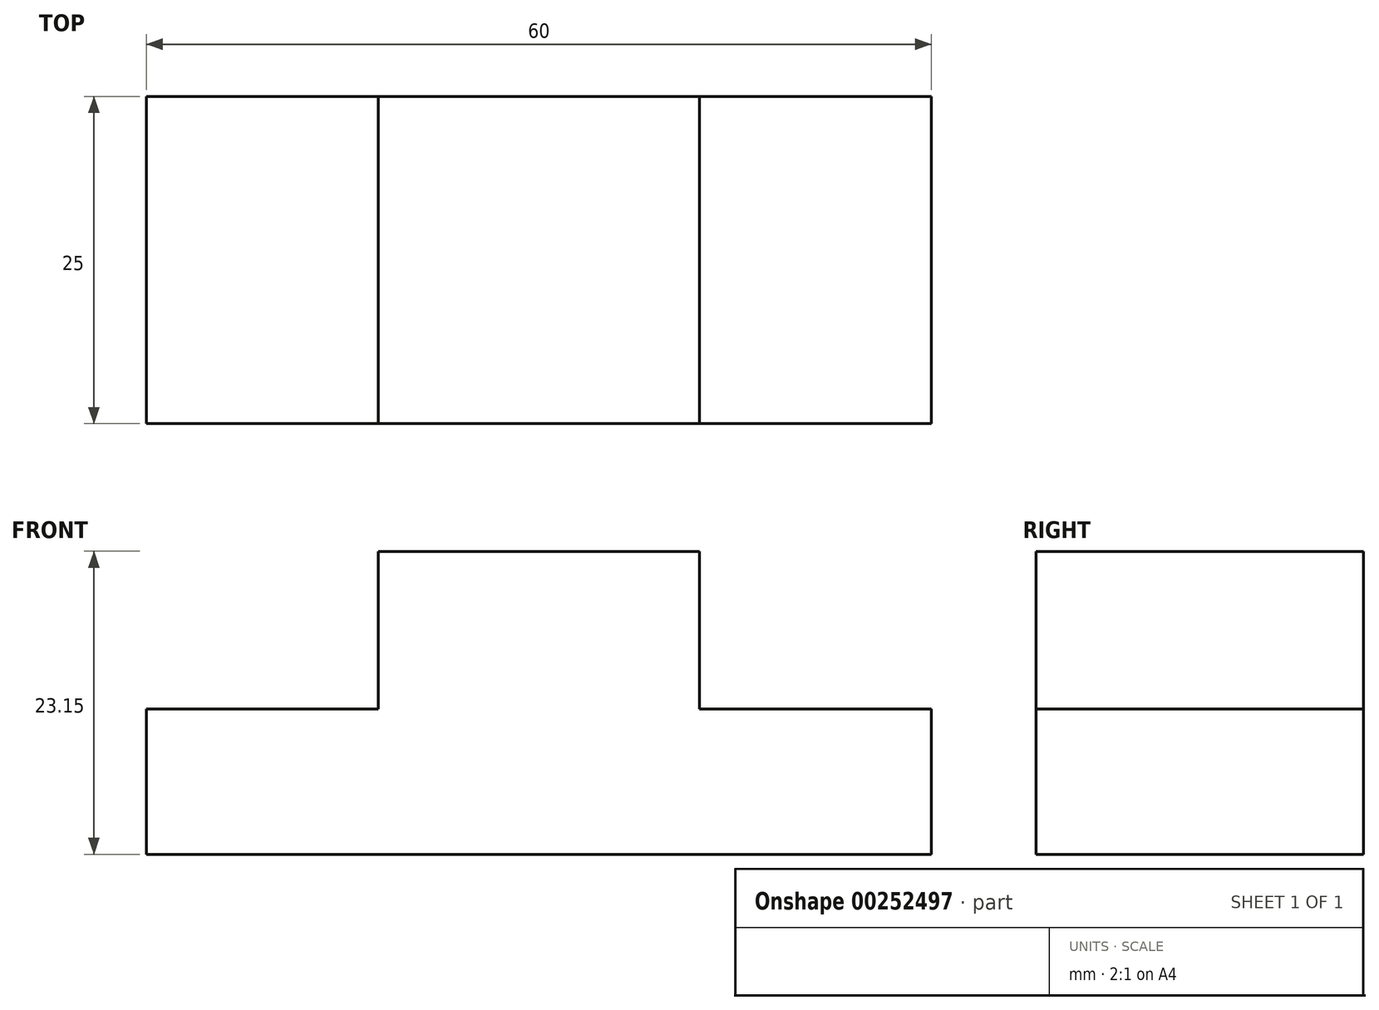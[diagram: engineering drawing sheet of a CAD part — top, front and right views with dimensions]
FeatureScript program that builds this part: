
annotation { "Feature Type Name" : "Feature", "Feature Type Description" : "" }
export const myFeature = defineFeature(function(context is Context, id is Id, definition is map)
    precondition{}
    {
        {
            var Q0;
            Q0=qCreatedBy(makeId("Front.planeOp"),FACE);
            var sketch = newSketch(context, id + "F0", { "sketchPlane" : qUnion([Q0])});
            skLineSegment(sketch, "E0.bottom", {"start": v(47.74, 36.53) * mm, "end": v(72.29, 36.53) * mm});
            skLineSegment(sketch, "E0.top", {"start": v(47.74, 48.58) * mm, "end": v(72.29, 48.58) * mm});
            skLineSegment(sketch, "E0.left", {"start": v(47.74, 36.53) * mm, "end": v(47.74, 48.58) * mm});
            skLineSegment(sketch, "E0.right", {"start": v(72.29, 36.53) * mm, "end": v(72.29, 48.58) * mm});
            skPoint(sketch, "E1", {"position": v(60.01, 36.53) * mm});
            skLineSegment(sketch, "E2.bottom", {"start": v(30.01, 25.43) * mm, "end": v(90.01, 25.43) * mm});
            skLineSegment(sketch, "E2.top", {"start": v(30.01, 36.53) * mm, "end": v(90.01, 36.53) * mm});
            skLineSegment(sketch, "E2.left", {"start": v(30.01, 25.43) * mm, "end": v(30.01, 36.53) * mm});
            skLineSegment(sketch, "E2.right", {"start": v(90.01, 25.43) * mm, "end": v(90.01, 36.53) * mm});
            skSolve(sketch);
        }
        {
            var Q0;
            Q0=makeQuery(id+"F0.imprint","IMPRINT",FACE,{"disambiguationData":[TD([[makeQuery(id+"F0.imprint","IMPRINT",EDGE,{"derivedFrom":sQuery(id+"F0.wireOp",EDGE,"E2.bottom")}),1.0]])]});
            var Q1;
            Q1=makeQuery(id+"F0.imprint","IMPRINT",FACE,{"disambiguationData":[TD([[makeQuery(id+"F0.imprint","IMPRINT",EDGE,{"derivedFrom":sQuery(id+"F0.wireOp",EDGE,"E0.top")}),-1.0]])]});
            extrude(context, id + "F1", {"entities" : qUnion([Q0, Q1]), "depth" : 25 * mm});
        }
    });
